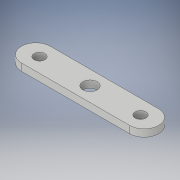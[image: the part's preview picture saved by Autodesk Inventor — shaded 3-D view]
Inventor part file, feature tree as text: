
AUTODESK INVENTOR PART (.ipt)
format: ipt  version: 2019 (Build 230136000, 136)  size: 112,128 bytes
history: native  units: mm
features: extrude x1, sketch x1
ambient origin geometry x8: Origin, YZ Plane, XZ Plane, XY Plane, X Axis, Y Axis, Z Axis, Center Point
bodies: Body1 (feature_tree)
feature tree (2):
  extrude  "Extrusión2"  Depth=14.0mm
  sketch  "Boceto1"  dims[d2=3.0mm d3=3.0mm d4=14.0mm d5=0.0mm d6=0.0mm d7=28.0mm d8=4.0mm d9=15.0mm d12=4.0mm d13=2.0mm d14=0.0mm]
